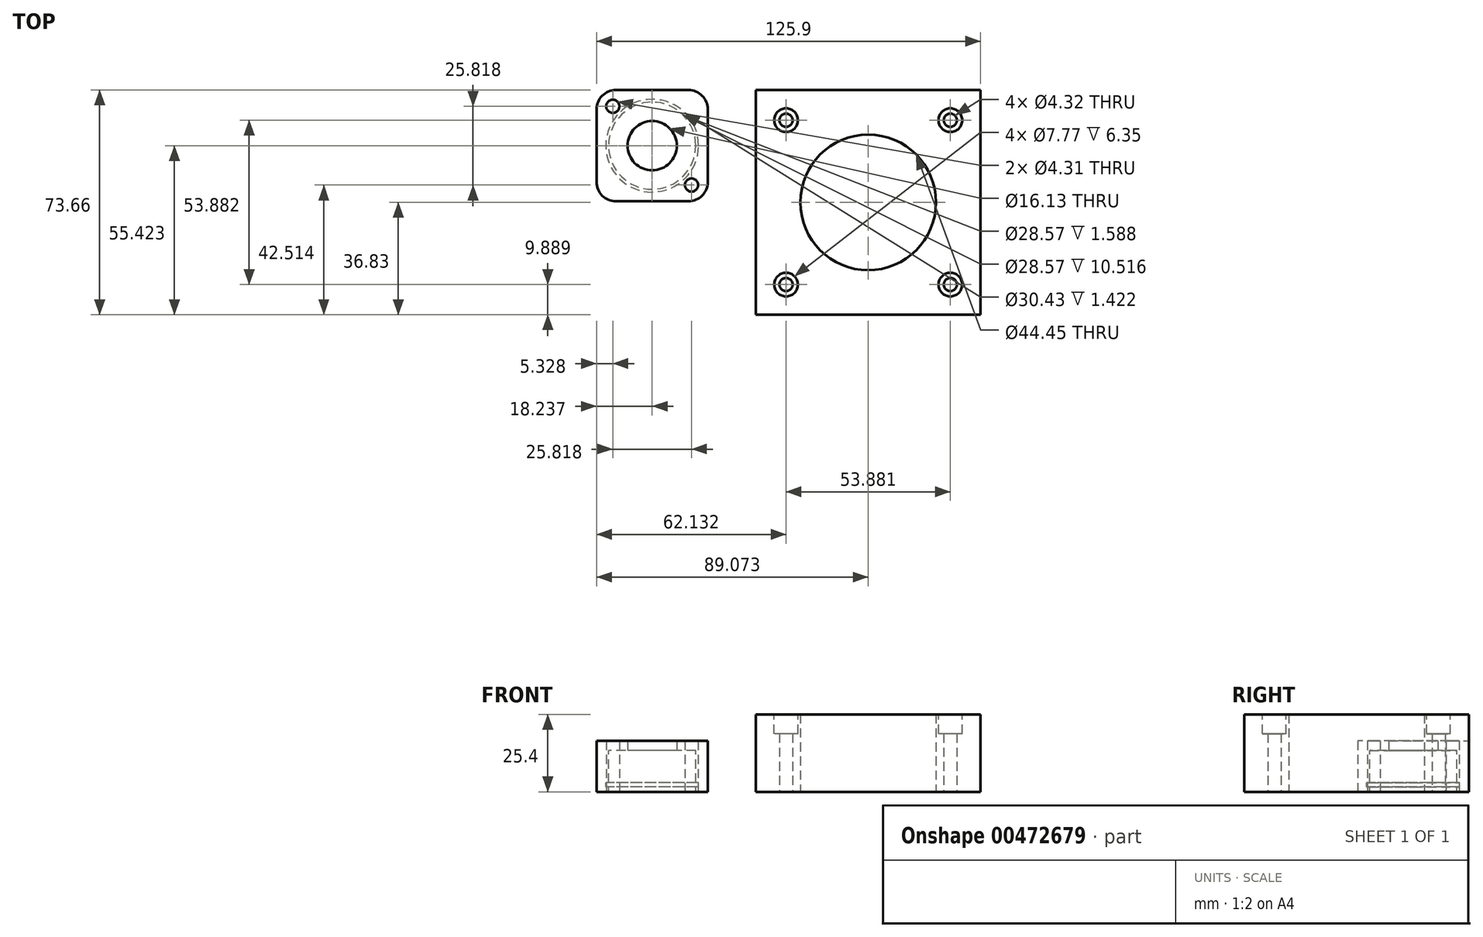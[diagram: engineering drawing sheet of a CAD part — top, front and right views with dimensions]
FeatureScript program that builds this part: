
annotation { "Feature Type Name" : "Feature", "Feature Type Description" : "" }
export const myFeature = defineFeature(function(context is Context, id is Id, definition is map)
    precondition{}
    {
        {
            var Q0;
            Q0=qCreatedBy(makeId("Top.planeOp"),FACE);
            var sketch = newSketch(context, id + "F0", { "sketchPlane" : qUnion([Q0])});
            skLineSegment(sketch, "E0.bottom", {"start": v(0, 0) * mm, "end": v(152.4, 0) * mm, "construction": true});
            skLineSegment(sketch, "E0.top", {"start": v(0, 152.4) * mm, "end": v(152.4, 152.4) * mm, "construction": true});
            skLineSegment(sketch, "E0.left", {"start": v(0, 0) * mm, "end": v(0, 152.4) * mm, "construction": true});
            skLineSegment(sketch, "E0.right", {"start": v(152.4, 0) * mm, "end": v(152.4, 152.4) * mm, "construction": true});
            skCircle(sketch, "E1", {"center": v(18.24, 134.16) * mm, "radius": 14.29 * mm});
            skCircle(sketch, "E2", {"center": v(18.24, 134.16) * mm, "radius": 8.06 * mm});
            skLineSegment(sketch, "E3", {"start": v(18.24, 134.16) * mm, "end": v(36.47, 134.16) * mm, "construction": true});
            skLineSegment(sketch, "E4", {"start": v(18.24, 134.16) * mm, "end": v(5.33, 147.07) * mm, "construction": true});
            skCircle(sketch, "E5", {"center": v(5.33, 147.07) * mm, "radius": 2.15 * mm});
            skCircle(sketch, "E6", {"center": v(18.24, 134.16) * mm, "radius": 18.26 * mm, "construction": true});
            skLineSegment(sketch, "E7.bottom", {"start": v(0, 152.4) * mm, "end": v(36.47, 152.4) * mm});
            skLineSegment(sketch, "E7.top", {"start": v(0, 115.93) * mm, "end": v(36.47, 115.93) * mm});
            skLineSegment(sketch, "E7.left", {"start": v(0, 152.4) * mm, "end": v(0, 115.93) * mm});
            skLineSegment(sketch, "E7.right", {"start": v(36.47, 152.4) * mm, "end": v(36.47, 115.93) * mm});
            skLineSegment(sketch, "E8.bottom", {"start": v(125.9, 152.4) * mm, "end": v(52.24, 152.4) * mm});
            skLineSegment(sketch, "E8.top", {"start": v(125.9, 78.74) * mm, "end": v(52.24, 78.74) * mm});
            skLineSegment(sketch, "E8.left", {"start": v(125.9, 152.4) * mm, "end": v(125.9, 78.74) * mm});
            skLineSegment(sketch, "E8.right", {"start": v(52.24, 152.4) * mm, "end": v(52.24, 78.74) * mm});
            skPoint(sketch, "E8.middle", {"position": v(89.07, 115.57) * mm});
            skCircle(sketch, "E9", {"center": v(62.13, 142.51) * mm, "radius": 2.16 * mm});
            skCircle(sketch, "E10", {"center": v(89.07, 115.57) * mm, "radius": 38.1 * mm, "construction": true});
            skCircle(sketch, "E11.1.0", {"center": v(62.13, 88.63) * mm, "radius": 2.16 * mm});
            skCircle(sketch, "E11.2.0", {"center": v(116.01, 88.63) * mm, "radius": 2.16 * mm});
            skCircle(sketch, "E11.3.0", {"center": v(116.01, 142.51) * mm, "radius": 2.16 * mm});
            skCircle(sketch, "E12", {"center": v(89.07, 115.57) * mm, "radius": 22.23 * mm});
            skLineSegment(sketch, "E13", {"start": v(89.07, 115.57) * mm, "end": v(62.13, 142.51) * mm, "construction": true});
            skLineSegment(sketch, "E14", {"start": v(18.24, 134.16) * mm, "end": v(5.33, 121.25) * mm, "construction": true});
            skCircle(sketch, "E15.MirrorC", {"center": v(31.15, 121.25) * mm, "radius": 2.15 * mm});
            skSolve(sketch);
        }
        {
            var Q0;
            Q0=makeQuery(id+"F0.imprint","IMPRINT",FACE,{"disambiguationData":[TD([[makeQuery(id+"F0.imprint","IMPRINT",EDGE,{"derivedFrom":sQuery(id+"F0.wireOp",EDGE,"E8.bottom")}),1.0]])]});
            extrude(context, id + "F1", {"entities" : qUnion([Q0]), "depth" : 25.4 * mm, "offsetDistance" : 25.4 * mm});
        }
        {
            var Q0;
            Q0=makeQuery(id+"F0.imprint","IMPRINT",FACE,{"disambiguationData":[TD([[makeQuery(id+"F0.imprint","IMPRINT",EDGE,{"derivedFrom":sQuery(id+"F0.wireOp",EDGE,"E1")}),-1.0]])]});
            var Q1;
            Q1=makeQuery(id+"F0.imprint","IMPRINT",FACE,{"disambiguationData":[TD([[makeQuery(id+"F0.imprint","IMPRINT",EDGE,{"derivedFrom":sQuery(id+"F0.wireOp",EDGE,"E1")}),1.0]])]});
            extrude(context, id + "F2", {"entities" : qUnion([Q0, Q1]), "depth" : 16.7 * mm, "offsetDistance" : 25.4 * mm});
        }
        {
            var Q0;
            Q0=makeQuery(id+"F1.opExtrude","CAP_FACE",FACE,{"disambiguationData":[OSD([sQuery(id+"F0.wireOp",EDGE,"E8.bottom"),sQuery(id+"F0.wireOp",EDGE,"E8.top"),sQuery(id+"F0.wireOp",EDGE,"E8.left"),sQuery(id+"F0.wireOp",EDGE,"E8.right"),sQuery(id+"F0.wireOp",EDGE,"E9"),sQuery(id+"F0.wireOp",EDGE,"E11.1.0"),sQuery(id+"F0.wireOp",EDGE,"E11.2.0"),sQuery(id+"F0.wireOp",EDGE,"E11.3.0"),sQuery(id+"F0.wireOp",EDGE,"E12")])],"isStart":false});
            var sketch = newSketch(context, id + "F3", { "sketchPlane" : qUnion([Q0])});
            skCircle(sketch, "E16", {"center": v(62.13, 142.51) * mm, "radius": 3.89 * mm});
            skPoint(sketch, "E17", {"position": v(89.07, 115.57) * mm});
            skCircle(sketch, "E18.1.0", {"center": v(62.13, 88.63) * mm, "radius": 3.89 * mm});
            skCircle(sketch, "E18.2.0", {"center": v(116.01, 88.63) * mm, "radius": 3.89 * mm});
            skCircle(sketch, "E18.3.0", {"center": v(116.01, 142.51) * mm, "radius": 3.89 * mm});
            skSolve(sketch);
        }
        {
            var Q0;
            Q0 = qSketchRegion(id + "F3", true);
            extrude(context, id + "F4", {"entities" : qUnion([Q0]), "operationType" : NewBodyOperationType.REMOVE, "oppositeDirection" : true, "depth" : 6.35 * mm});
        }
        {
            var Q0;
            Q0=sQuery(id+"F0.wireOp",EDGE,"E4");
            var Q1;
            Q1=sQuery(id+"F0.wireOp",VERTEX,"E1.center");
            cPlane(context, id + "F5", {"entities" : qUnion([Q0, Q1]), "cplaneType" : CPlaneType.LINE_POINT, "offset" : 25.4 * mm, "width" : 152.4 * mm, "height" : 152.4 * mm});
        }
        {
            var Q0;
            Q0=qCreatedBy(id+"F5.planeOp",FACE);
            var sketch = newSketch(context, id + "F6", { "sketchPlane" : qUnion([Q0])});
            skLineSegment(sketch, "E19", {"start": v(-107.76, 0) * mm, "end": v(-107.76, 16.7) * mm});
            skLineSegment(sketch, "E20", {"start": v(-122.05, 0) * mm, "end": v(-122.05, 1.59) * mm});
            skLineSegment(sketch, "E21", {"start": v(-122.05, 1.59) * mm, "end": v(-122.98, 1.59) * mm});
            skLineSegment(sketch, "E22", {"start": v(-122.98, 1.59) * mm, "end": v(-122.98, 3) * mm});
            skLineSegment(sketch, "E23", {"start": v(-122.98, 3) * mm, "end": v(-122.05, 3) * mm});
            skLineSegment(sketch, "E24", {"start": v(-122.05, 3) * mm, "end": v(-122.05, 13.53) * mm});
            skLineSegment(sketch, "E25", {"start": v(-122.05, 13.53) * mm, "end": v(-115.83, 13.53) * mm});
            skLineSegment(sketch, "E26", {"start": v(-115.83, 13.53) * mm, "end": v(-115.83, 16.7) * mm});
            skLineSegment(sketch, "E27", {"start": v(-115.83, 16.7) * mm, "end": v(-107.76, 16.7) * mm});
            skLineSegment(sketch, "E28", {"start": v(-122.05, 0) * mm, "end": v(-107.76, 0) * mm});
            skLineSegment(sketch, "E29", {"start": v(-115.83, 13.53) * mm, "end": v(-115.83, 0) * mm, "construction": true});
            skSolve(sketch);
        }
        {
            var Q0;
            Q0 = qSketchRegion(id + "F6", true);
            var Q1;
            Q1=sQuery(id+"F6.wireOp",EDGE,"E19");
            revolve(context, id + "F7", {"operationType" : NewBodyOperationType.REMOVE, "entities" : qUnion([Q0]), "axis" : qUnion([Q1]), "revolveType" : RevolveType.FULL, "oppositeDirection" : true});
        }
        {
            var Q0;
            Q0=makeQuery(id+"F2.opExtrude","SWEPT_EDGE",EDGE,{"disambiguationData":[OSD([sQuery(id+"F0.wireOp",EDGE,"E7.bottom"),sQuery(id+"F0.wireOp",EDGE,"E7.left")])]});
            var Q1;
            Q1=makeQuery(id+"F2.opExtrude","SWEPT_EDGE",EDGE,{"disambiguationData":[OSD([sQuery(id+"F0.wireOp",EDGE,"E7.bottom"),sQuery(id+"F0.wireOp",EDGE,"E7.right")])]});
            var Q2;
            Q2=makeQuery(id+"F2.opExtrude","SWEPT_EDGE",EDGE,{"disambiguationData":[OSD([sQuery(id+"F0.wireOp",EDGE,"E7.top"),sQuery(id+"F0.wireOp",EDGE,"E7.right")])]});
            var Q3;
            Q3=makeQuery(id+"F2.opExtrude","SWEPT_EDGE",EDGE,{"disambiguationData":[OSD([sQuery(id+"F0.wireOp",EDGE,"E7.top"),sQuery(id+"F0.wireOp",EDGE,"E7.left")])]});
            fillet(context, id + "F8", {"entities" : qUnion([Q0, Q1, Q2, Q3]), "radius" : 6.35 * mm, "tangentPropagation" : true, "allowEdgeOverflow" : false});
        }
    });
